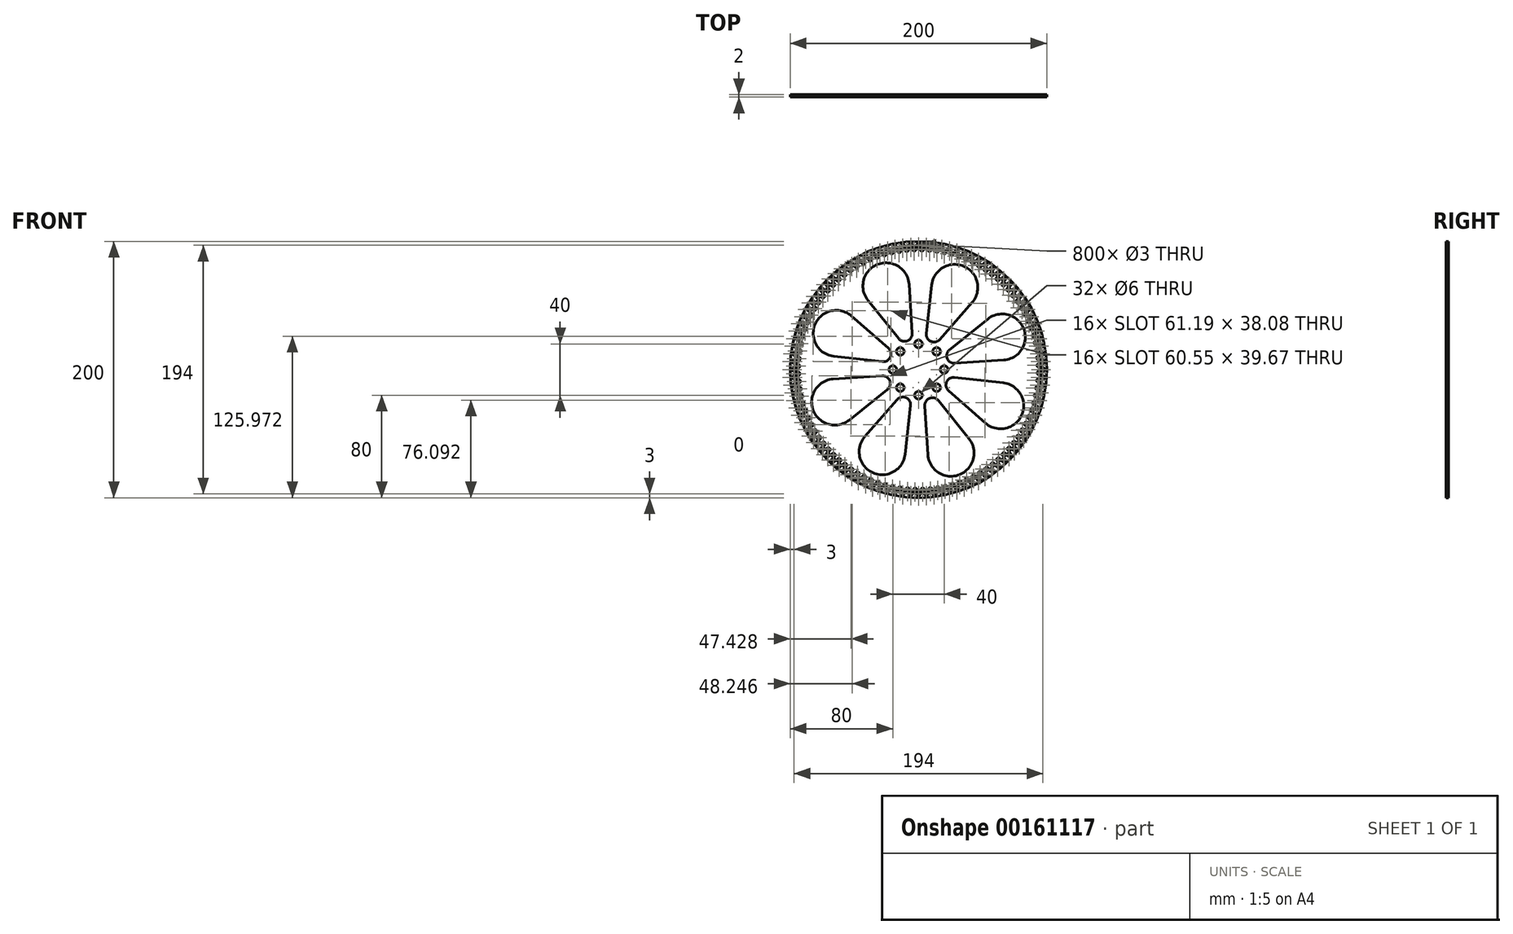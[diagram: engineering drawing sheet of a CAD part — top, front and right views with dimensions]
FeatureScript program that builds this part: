
annotation { "Feature Type Name" : "Feature", "Feature Type Description" : "" }
export const myFeature = defineFeature(function(context is Context, id is Id, definition is map)
    precondition{}
    {
        {
            var Q0;
            Q0=qCreatedBy(makeId("Front.planeOp"),FACE);
            var sketch = newSketch(context, id + "F0", { "sketchPlane" : qUnion([Q0])});
            skCircle(sketch, "E0", {"center": v(0, 0) * mm, "radius": 100 * mm});
            skCircle(sketch, "E1", {"center": v(0, 20) * mm, "radius": 3 * mm});
            skCircle(sketch, "E2.1.0", {"center": v(-14.14, 14.14) * mm, "radius": 3 * mm});
            skCircle(sketch, "E2.2.0", {"center": v(-20, 0) * mm, "radius": 3 * mm});
            skCircle(sketch, "E2.3.0", {"center": v(-14.14, -14.14) * mm, "radius": 3 * mm});
            skCircle(sketch, "E2.4.0", {"center": v(0, -20) * mm, "radius": 3 * mm});
            skCircle(sketch, "E2.5.0", {"center": v(14.14, -14.14) * mm, "radius": 3 * mm});
            skCircle(sketch, "E2.6.0", {"center": v(20, 0) * mm, "radius": 3 * mm});
            skCircle(sketch, "E2.7.0", {"center": v(14.14, 14.14) * mm, "radius": 3 * mm});
            skCircle(sketch, "E3", {"center": v(0, 97) * mm, "radius": 1.5 * mm});
            skCircle(sketch, "E4.1.0", {"center": v(-6.1, 96.8) * mm, "radius": 1.5 * mm});
            skCircle(sketch, "E4.2.0", {"center": v(-12.16, 96.24) * mm, "radius": 1.5 * mm});
            skCircle(sketch, "E4.3.0", {"center": v(-18.18, 95.28) * mm, "radius": 1.5 * mm});
            skCircle(sketch, "E4.4.0", {"center": v(-24.12, 93.95) * mm, "radius": 1.5 * mm});
            skCircle(sketch, "E4.5.0", {"center": v(-29.97, 92.25) * mm, "radius": 1.5 * mm});
            skCircle(sketch, "E4.6.0", {"center": v(-35.7, 90.19) * mm, "radius": 1.5 * mm});
            skCircle(sketch, "E4.7.0", {"center": v(-41.3, 87.77) * mm, "radius": 1.5 * mm});
            skCircle(sketch, "E4.8.0", {"center": v(-46.73, 85) * mm, "radius": 1.5 * mm});
            skCircle(sketch, "E4.9.0", {"center": v(-51.98, 81.9) * mm, "radius": 1.5 * mm});
            skCircle(sketch, "E4.10.0", {"center": v(-57.02, 78.47) * mm, "radius": 1.5 * mm});
            skCircle(sketch, "E4.11.0", {"center": v(-61.83, 74.74) * mm, "radius": 1.5 * mm});
            skCircle(sketch, "E4.12.0", {"center": v(-66.4, 70.7) * mm, "radius": 1.5 * mm});
            skCircle(sketch, "E4.13.0", {"center": v(-70.7, 66.4) * mm, "radius": 1.5 * mm});
            skCircle(sketch, "E4.14.0", {"center": v(-74.74, 61.83) * mm, "radius": 1.5 * mm});
            skCircle(sketch, "E4.15.0", {"center": v(-78.47, 57.02) * mm, "radius": 1.5 * mm});
            skCircle(sketch, "E4.16.0", {"center": v(-81.9, 51.98) * mm, "radius": 1.5 * mm});
            skCircle(sketch, "E4.17.0", {"center": v(-85, 46.73) * mm, "radius": 1.5 * mm});
            skCircle(sketch, "E4.18.0", {"center": v(-87.77, 41.3) * mm, "radius": 1.5 * mm});
            skCircle(sketch, "E4.19.0", {"center": v(-90.19, 35.7) * mm, "radius": 1.5 * mm});
            skCircle(sketch, "E4.20.0", {"center": v(-92.25, 29.97) * mm, "radius": 1.5 * mm});
            skCircle(sketch, "E4.21.0", {"center": v(-93.95, 24.12) * mm, "radius": 1.5 * mm});
            skCircle(sketch, "E4.22.0", {"center": v(-95.28, 18.18) * mm, "radius": 1.5 * mm});
            skCircle(sketch, "E4.23.0", {"center": v(-96.24, 12.16) * mm, "radius": 1.5 * mm});
            skCircle(sketch, "E4.24.0", {"center": v(-96.8, 6.1) * mm, "radius": 1.5 * mm});
            skCircle(sketch, "E4.25.0", {"center": v(-97, 0) * mm, "radius": 1.5 * mm});
            skCircle(sketch, "E4.26.0", {"center": v(-96.8, -6.1) * mm, "radius": 1.5 * mm});
            skCircle(sketch, "E4.27.0", {"center": v(-96.24, -12.16) * mm, "radius": 1.5 * mm});
            skCircle(sketch, "E4.28.0", {"center": v(-95.28, -18.18) * mm, "radius": 1.5 * mm});
            skCircle(sketch, "E4.29.0", {"center": v(-93.95, -24.12) * mm, "radius": 1.5 * mm});
            skCircle(sketch, "E4.30.0", {"center": v(-92.25, -29.97) * mm, "radius": 1.5 * mm});
            skCircle(sketch, "E4.31.0", {"center": v(-90.19, -35.7) * mm, "radius": 1.5 * mm});
            skCircle(sketch, "E4.32.0", {"center": v(-87.77, -41.3) * mm, "radius": 1.5 * mm});
            skCircle(sketch, "E4.33.0", {"center": v(-85, -46.73) * mm, "radius": 1.5 * mm});
            skCircle(sketch, "E4.34.0", {"center": v(-81.9, -51.98) * mm, "radius": 1.5 * mm});
            skCircle(sketch, "E4.35.0", {"center": v(-78.47, -57.02) * mm, "radius": 1.5 * mm});
            skCircle(sketch, "E4.36.0", {"center": v(-74.74, -61.83) * mm, "radius": 1.5 * mm});
            skCircle(sketch, "E4.37.0", {"center": v(-70.7, -66.4) * mm, "radius": 1.5 * mm});
            skCircle(sketch, "E4.38.0", {"center": v(-66.4, -70.7) * mm, "radius": 1.5 * mm});
            skCircle(sketch, "E4.39.0", {"center": v(-61.83, -74.74) * mm, "radius": 1.5 * mm});
            skCircle(sketch, "E4.40.0", {"center": v(-57.02, -78.47) * mm, "radius": 1.5 * mm});
            skCircle(sketch, "E4.41.0", {"center": v(-51.98, -81.9) * mm, "radius": 1.5 * mm});
            skCircle(sketch, "E4.42.0", {"center": v(-46.73, -85) * mm, "radius": 1.5 * mm});
            skCircle(sketch, "E4.43.0", {"center": v(-41.3, -87.77) * mm, "radius": 1.5 * mm});
            skCircle(sketch, "E4.44.0", {"center": v(-35.7, -90.19) * mm, "radius": 1.5 * mm});
            skCircle(sketch, "E4.45.0", {"center": v(-29.97, -92.25) * mm, "radius": 1.5 * mm});
            skCircle(sketch, "E4.46.0", {"center": v(-24.12, -93.95) * mm, "radius": 1.5 * mm});
            skCircle(sketch, "E4.47.0", {"center": v(-18.18, -95.28) * mm, "radius": 1.5 * mm});
            skCircle(sketch, "E4.48.0", {"center": v(-12.16, -96.24) * mm, "radius": 1.5 * mm});
            skCircle(sketch, "E4.49.0", {"center": v(-6.1, -96.8) * mm, "radius": 1.5 * mm});
            skCircle(sketch, "E4.50.0", {"center": v(0, -97) * mm, "radius": 1.5 * mm});
            skCircle(sketch, "E4.51.0", {"center": v(6.1, -96.8) * mm, "radius": 1.5 * mm});
            skCircle(sketch, "E4.52.0", {"center": v(12.16, -96.24) * mm, "radius": 1.5 * mm});
            skCircle(sketch, "E4.53.0", {"center": v(18.18, -95.28) * mm, "radius": 1.5 * mm});
            skCircle(sketch, "E4.54.0", {"center": v(24.12, -93.95) * mm, "radius": 1.5 * mm});
            skCircle(sketch, "E4.55.0", {"center": v(29.97, -92.25) * mm, "radius": 1.5 * mm});
            skCircle(sketch, "E4.56.0", {"center": v(35.7, -90.19) * mm, "radius": 1.5 * mm});
            skCircle(sketch, "E4.57.0", {"center": v(41.3, -87.77) * mm, "radius": 1.5 * mm});
            skCircle(sketch, "E4.58.0", {"center": v(46.73, -85) * mm, "radius": 1.5 * mm});
            skCircle(sketch, "E4.59.0", {"center": v(51.98, -81.9) * mm, "radius": 1.5 * mm});
            skCircle(sketch, "E4.60.0", {"center": v(57.02, -78.47) * mm, "radius": 1.5 * mm});
            skCircle(sketch, "E4.61.0", {"center": v(61.83, -74.74) * mm, "radius": 1.5 * mm});
            skCircle(sketch, "E4.62.0", {"center": v(66.4, -70.7) * mm, "radius": 1.5 * mm});
            skCircle(sketch, "E4.63.0", {"center": v(70.7, -66.4) * mm, "radius": 1.5 * mm});
            skCircle(sketch, "E4.64.0", {"center": v(74.74, -61.83) * mm, "radius": 1.5 * mm});
            skCircle(sketch, "E4.65.0", {"center": v(78.47, -57.02) * mm, "radius": 1.5 * mm});
            skCircle(sketch, "E4.66.0", {"center": v(81.9, -51.98) * mm, "radius": 1.5 * mm});
            skCircle(sketch, "E4.67.0", {"center": v(85, -46.73) * mm, "radius": 1.5 * mm});
            skCircle(sketch, "E4.68.0", {"center": v(87.77, -41.3) * mm, "radius": 1.5 * mm});
            skCircle(sketch, "E4.69.0", {"center": v(90.19, -35.7) * mm, "radius": 1.5 * mm});
            skCircle(sketch, "E4.70.0", {"center": v(92.25, -29.97) * mm, "radius": 1.5 * mm});
            skCircle(sketch, "E4.71.0", {"center": v(93.95, -24.12) * mm, "radius": 1.5 * mm});
            skCircle(sketch, "E4.72.0", {"center": v(95.28, -18.18) * mm, "radius": 1.5 * mm});
            skCircle(sketch, "E4.73.0", {"center": v(96.24, -12.16) * mm, "radius": 1.5 * mm});
            skCircle(sketch, "E4.74.0", {"center": v(96.8, -6.1) * mm, "radius": 1.5 * mm});
            skCircle(sketch, "E4.75.0", {"center": v(97, 0) * mm, "radius": 1.5 * mm});
            skCircle(sketch, "E4.76.0", {"center": v(96.8, 6.1) * mm, "radius": 1.5 * mm});
            skCircle(sketch, "E4.77.0", {"center": v(96.24, 12.16) * mm, "radius": 1.5 * mm});
            skCircle(sketch, "E4.78.0", {"center": v(95.28, 18.18) * mm, "radius": 1.5 * mm});
            skCircle(sketch, "E4.79.0", {"center": v(93.95, 24.12) * mm, "radius": 1.5 * mm});
            skCircle(sketch, "E4.80.0", {"center": v(92.25, 29.97) * mm, "radius": 1.5 * mm});
            skCircle(sketch, "E4.81.0", {"center": v(90.19, 35.7) * mm, "radius": 1.5 * mm});
            skCircle(sketch, "E4.82.0", {"center": v(87.77, 41.3) * mm, "radius": 1.5 * mm});
            skCircle(sketch, "E4.83.0", {"center": v(85, 46.73) * mm, "radius": 1.5 * mm});
            skCircle(sketch, "E4.84.0", {"center": v(81.9, 51.98) * mm, "radius": 1.5 * mm});
            skCircle(sketch, "E4.85.0", {"center": v(78.47, 57.02) * mm, "radius": 1.5 * mm});
            skCircle(sketch, "E4.86.0", {"center": v(74.74, 61.83) * mm, "radius": 1.5 * mm});
            skCircle(sketch, "E4.87.0", {"center": v(70.7, 66.4) * mm, "radius": 1.5 * mm});
            skCircle(sketch, "E4.88.0", {"center": v(66.4, 70.7) * mm, "radius": 1.5 * mm});
            skCircle(sketch, "E4.89.0", {"center": v(61.83, 74.74) * mm, "radius": 1.5 * mm});
            skCircle(sketch, "E4.90.0", {"center": v(57.02, 78.47) * mm, "radius": 1.5 * mm});
            skCircle(sketch, "E4.91.0", {"center": v(51.98, 81.9) * mm, "radius": 1.5 * mm});
            skCircle(sketch, "E4.92.0", {"center": v(46.73, 85) * mm, "radius": 1.5 * mm});
            skCircle(sketch, "E4.93.0", {"center": v(41.3, 87.77) * mm, "radius": 1.5 * mm});
            skCircle(sketch, "E4.94.0", {"center": v(35.7, 90.19) * mm, "radius": 1.5 * mm});
            skCircle(sketch, "E4.95.0", {"center": v(29.97, 92.25) * mm, "radius": 1.5 * mm});
            skCircle(sketch, "E4.96.0", {"center": v(24.12, 93.95) * mm, "radius": 1.5 * mm});
            skCircle(sketch, "E4.97.0", {"center": v(18.18, 95.28) * mm, "radius": 1.5 * mm});
            skCircle(sketch, "E4.98.0", {"center": v(12.16, 96.24) * mm, "radius": 1.5 * mm});
            skCircle(sketch, "E4.99.0", {"center": v(6.1, 96.8) * mm, "radius": 1.5 * mm});
            skCircle(sketch, "E5", {"center": v(2.62, 93.96) * mm, "radius": 1.5 * mm});
            skLineSegment(sketch, "E6", {"start": v(0, 97) * mm, "end": v(0, 0) * mm, "construction": true});
            skLineSegment(sketch, "E7", {"start": v(2.62, 93.96) * mm, "end": v(0, 0) * mm, "construction": true});
            skCircle(sketch, "E8.1.0", {"center": v(-3.28, 93.94) * mm, "radius": 1.5 * mm});
            skCircle(sketch, "E8.2.0", {"center": v(-9.17, 93.55) * mm, "radius": 1.5 * mm});
            skCircle(sketch, "E9.1.3.0", {"center": v(-15.03, 92.8) * mm, "radius": 1.5 * mm});
            skCircle(sketch, "E9.1.4.0", {"center": v(-20.83, 91.66) * mm, "radius": 1.5 * mm});
            skCircle(sketch, "E9.1.5.0", {"center": v(-26.54, 90.18) * mm, "radius": 1.5 * mm});
            skCircle(sketch, "E9.1.6.0", {"center": v(-32.15, 88.33) * mm, "radius": 1.5 * mm});
            skCircle(sketch, "E9.1.7.0", {"center": v(-37.63, 86.14) * mm, "radius": 1.5 * mm});
            skCircle(sketch, "E9.1.8.0", {"center": v(-42.97, 83.6) * mm, "radius": 1.5 * mm});
            skCircle(sketch, "E9.1.9.0", {"center": v(-48.13, 80.74) * mm, "radius": 1.5 * mm});
            skCircle(sketch, "E9.1.10.0", {"center": v(-53.1, 77.56) * mm, "radius": 1.5 * mm});
            skCircle(sketch, "E9.1.11.0", {"center": v(-57.87, 74.07) * mm, "radius": 1.5 * mm});
            skCircle(sketch, "E9.1.12.0", {"center": v(-62.4, 70.3) * mm, "radius": 1.5 * mm});
            skCircle(sketch, "E9.1.13.0", {"center": v(-66.7, 66.24) * mm, "radius": 1.5 * mm});
            skCircle(sketch, "E9.1.14.0", {"center": v(-70.73, 61.92) * mm, "radius": 1.5 * mm});
            skCircle(sketch, "E9.1.15.0", {"center": v(-74.48, 57.35) * mm, "radius": 1.5 * mm});
            skCircle(sketch, "E9.1.16.0", {"center": v(-77.93, 52.56) * mm, "radius": 1.5 * mm});
            skCircle(sketch, "E9.1.17.0", {"center": v(-81.08, 47.57) * mm, "radius": 1.5 * mm});
            skCircle(sketch, "E9.1.18.0", {"center": v(-83.9, 42.38) * mm, "radius": 1.5 * mm});
            skCircle(sketch, "E9.1.19.0", {"center": v(-86.4, 37.03) * mm, "radius": 1.5 * mm});
            skCircle(sketch, "E9.1.20.0", {"center": v(-88.55, 31.53) * mm, "radius": 1.5 * mm});
            skCircle(sketch, "E9.1.21.0", {"center": v(-90.36, 25.9) * mm, "radius": 1.5 * mm});
            skCircle(sketch, "E9.1.22.0", {"center": v(-91.8, 20.19) * mm, "radius": 1.5 * mm});
            skCircle(sketch, "E9.1.23.0", {"center": v(-92.9, 14.38) * mm, "radius": 1.5 * mm});
            skCircle(sketch, "E9.1.24.0", {"center": v(-93.61, 8.52) * mm, "radius": 1.5 * mm});
            skCircle(sketch, "E9.1.25.0", {"center": v(-93.96, 2.62) * mm, "radius": 1.5 * mm});
            skCircle(sketch, "E9.1.26.0", {"center": v(-93.94, -3.28) * mm, "radius": 1.5 * mm});
            skCircle(sketch, "E9.1.27.0", {"center": v(-93.55, -9.17) * mm, "radius": 1.5 * mm});
            skCircle(sketch, "E9.1.28.0", {"center": v(-92.8, -15.03) * mm, "radius": 1.5 * mm});
            skCircle(sketch, "E9.1.29.0", {"center": v(-91.66, -20.83) * mm, "radius": 1.5 * mm});
            skCircle(sketch, "E9.1.30.0", {"center": v(-90.18, -26.54) * mm, "radius": 1.5 * mm});
            skCircle(sketch, "E9.1.31.0", {"center": v(-88.33, -32.15) * mm, "radius": 1.5 * mm});
            skCircle(sketch, "E9.1.32.0", {"center": v(-86.14, -37.63) * mm, "radius": 1.5 * mm});
            skCircle(sketch, "E9.1.33.0", {"center": v(-83.6, -42.97) * mm, "radius": 1.5 * mm});
            skCircle(sketch, "E9.1.34.0", {"center": v(-80.74, -48.13) * mm, "radius": 1.5 * mm});
            skCircle(sketch, "E9.1.35.0", {"center": v(-77.56, -53.1) * mm, "radius": 1.5 * mm});
            skCircle(sketch, "E9.1.36.0", {"center": v(-74.07, -57.87) * mm, "radius": 1.5 * mm});
            skCircle(sketch, "E9.1.37.0", {"center": v(-70.3, -62.4) * mm, "radius": 1.5 * mm});
            skCircle(sketch, "E9.1.38.0", {"center": v(-66.24, -66.7) * mm, "radius": 1.5 * mm});
            skCircle(sketch, "E9.1.39.0", {"center": v(-61.92, -70.73) * mm, "radius": 1.5 * mm});
            skCircle(sketch, "E9.1.40.0", {"center": v(-57.35, -74.48) * mm, "radius": 1.5 * mm});
            skCircle(sketch, "E9.1.41.0", {"center": v(-52.56, -77.93) * mm, "radius": 1.5 * mm});
            skCircle(sketch, "E9.1.42.0", {"center": v(-47.57, -81.08) * mm, "radius": 1.5 * mm});
            skCircle(sketch, "E9.1.43.0", {"center": v(-42.38, -83.9) * mm, "radius": 1.5 * mm});
            skCircle(sketch, "E9.1.44.0", {"center": v(-37.03, -86.4) * mm, "radius": 1.5 * mm});
            skCircle(sketch, "E9.1.45.0", {"center": v(-31.53, -88.55) * mm, "radius": 1.5 * mm});
            skCircle(sketch, "E9.1.46.0", {"center": v(-25.9, -90.36) * mm, "radius": 1.5 * mm});
            skCircle(sketch, "E9.1.47.0", {"center": v(-20.19, -91.8) * mm, "radius": 1.5 * mm});
            skCircle(sketch, "E9.1.48.0", {"center": v(-14.38, -92.9) * mm, "radius": 1.5 * mm});
            skCircle(sketch, "E9.1.49.0", {"center": v(-8.52, -93.61) * mm, "radius": 1.5 * mm});
            skCircle(sketch, "E9.1.50.0", {"center": v(-2.62, -93.96) * mm, "radius": 1.5 * mm});
            skCircle(sketch, "E9.1.51.0", {"center": v(3.28, -93.94) * mm, "radius": 1.5 * mm});
            skCircle(sketch, "E9.1.52.0", {"center": v(9.17, -93.55) * mm, "radius": 1.5 * mm});
            skCircle(sketch, "E9.1.53.0", {"center": v(15.03, -92.8) * mm, "radius": 1.5 * mm});
            skCircle(sketch, "E9.1.54.0", {"center": v(20.83, -91.66) * mm, "radius": 1.5 * mm});
            skCircle(sketch, "E9.1.55.0", {"center": v(26.54, -90.18) * mm, "radius": 1.5 * mm});
            skCircle(sketch, "E9.1.56.0", {"center": v(32.15, -88.33) * mm, "radius": 1.5 * mm});
            skCircle(sketch, "E9.1.57.0", {"center": v(37.63, -86.14) * mm, "radius": 1.5 * mm});
            skCircle(sketch, "E9.1.58.0", {"center": v(42.97, -83.6) * mm, "radius": 1.5 * mm});
            skCircle(sketch, "E9.1.59.0", {"center": v(48.13, -80.74) * mm, "radius": 1.5 * mm});
            skCircle(sketch, "E9.1.60.0", {"center": v(53.1, -77.56) * mm, "radius": 1.5 * mm});
            skCircle(sketch, "E9.1.61.0", {"center": v(57.87, -74.07) * mm, "radius": 1.5 * mm});
            skCircle(sketch, "E9.1.62.0", {"center": v(62.4, -70.3) * mm, "radius": 1.5 * mm});
            skCircle(sketch, "E9.1.63.0", {"center": v(66.7, -66.24) * mm, "radius": 1.5 * mm});
            skCircle(sketch, "E9.1.64.0", {"center": v(70.73, -61.92) * mm, "radius": 1.5 * mm});
            skCircle(sketch, "E9.1.65.0", {"center": v(74.48, -57.35) * mm, "radius": 1.5 * mm});
            skCircle(sketch, "E9.1.66.0", {"center": v(77.93, -52.56) * mm, "radius": 1.5 * mm});
            skCircle(sketch, "E9.1.67.0", {"center": v(81.08, -47.57) * mm, "radius": 1.5 * mm});
            skCircle(sketch, "E9.1.68.0", {"center": v(83.9, -42.38) * mm, "radius": 1.5 * mm});
            skCircle(sketch, "E9.1.69.0", {"center": v(86.4, -37.03) * mm, "radius": 1.5 * mm});
            skCircle(sketch, "E9.1.70.0", {"center": v(88.55, -31.53) * mm, "radius": 1.5 * mm});
            skCircle(sketch, "E9.1.71.0", {"center": v(90.36, -25.9) * mm, "radius": 1.5 * mm});
            skCircle(sketch, "E9.1.72.0", {"center": v(91.8, -20.19) * mm, "radius": 1.5 * mm});
            skCircle(sketch, "E9.1.73.0", {"center": v(92.9, -14.38) * mm, "radius": 1.5 * mm});
            skCircle(sketch, "E9.1.74.0", {"center": v(93.61, -8.52) * mm, "radius": 1.5 * mm});
            skCircle(sketch, "E9.1.75.0", {"center": v(93.96, -2.62) * mm, "radius": 1.5 * mm});
            skCircle(sketch, "E9.1.76.0", {"center": v(93.94, 3.28) * mm, "radius": 1.5 * mm});
            skCircle(sketch, "E9.1.77.0", {"center": v(93.55, 9.17) * mm, "radius": 1.5 * mm});
            skCircle(sketch, "E9.1.78.0", {"center": v(92.8, 15.03) * mm, "radius": 1.5 * mm});
            skCircle(sketch, "E9.1.79.0", {"center": v(91.66, 20.83) * mm, "radius": 1.5 * mm});
            skCircle(sketch, "E9.1.80.0", {"center": v(90.18, 26.54) * mm, "radius": 1.5 * mm});
            skCircle(sketch, "E9.1.81.0", {"center": v(88.33, 32.15) * mm, "radius": 1.5 * mm});
            skCircle(sketch, "E9.1.82.0", {"center": v(86.14, 37.63) * mm, "radius": 1.5 * mm});
            skCircle(sketch, "E9.1.83.0", {"center": v(83.6, 42.97) * mm, "radius": 1.5 * mm});
            skCircle(sketch, "E9.1.84.0", {"center": v(80.74, 48.13) * mm, "radius": 1.5 * mm});
            skCircle(sketch, "E9.1.85.0", {"center": v(77.56, 53.1) * mm, "radius": 1.5 * mm});
            skCircle(sketch, "E9.1.86.0", {"center": v(74.07, 57.87) * mm, "radius": 1.5 * mm});
            skCircle(sketch, "E9.1.87.0", {"center": v(70.3, 62.4) * mm, "radius": 1.5 * mm});
            skCircle(sketch, "E9.1.88.0", {"center": v(66.24, 66.7) * mm, "radius": 1.5 * mm});
            skCircle(sketch, "E9.1.89.0", {"center": v(61.92, 70.73) * mm, "radius": 1.5 * mm});
            skCircle(sketch, "E9.1.90.0", {"center": v(57.35, 74.48) * mm, "radius": 1.5 * mm});
            skCircle(sketch, "E9.1.91.0", {"center": v(52.56, 77.93) * mm, "radius": 1.5 * mm});
            skCircle(sketch, "E9.1.92.0", {"center": v(47.57, 81.08) * mm, "radius": 1.5 * mm});
            skCircle(sketch, "E9.1.93.0", {"center": v(42.38, 83.9) * mm, "radius": 1.5 * mm});
            skCircle(sketch, "E9.1.94.0", {"center": v(37.03, 86.4) * mm, "radius": 1.5 * mm});
            skCircle(sketch, "E9.1.95.0", {"center": v(31.53, 88.55) * mm, "radius": 1.5 * mm});
            skCircle(sketch, "E9.1.96.0", {"center": v(25.9, 90.36) * mm, "radius": 1.5 * mm});
            skCircle(sketch, "E9.1.97.0", {"center": v(20.19, 91.8) * mm, "radius": 1.5 * mm});
            skCircle(sketch, "E9.1.98.0", {"center": v(14.38, 92.9) * mm, "radius": 1.5 * mm});
            skCircle(sketch, "E9.1.99.0", {"center": v(8.52, 93.61) * mm, "radius": 1.5 * mm});
            skArc(sketch, "E10", {"start": v(-28.11, 6.14) * mm, "mid": v(-21.96, 9.68) * mm, "end": v(-23.5, 16.61) * mm});
            skArc(sketch, "E11", {"start": v(-52.19, 41.77) * mm, "mid": v(-80.52, 35.5) * mm, "end": v(-66.04, 10.34) * mm});
            skLineSegment(sketch, "E12", {"start": v(-28.11, 6.14) * mm, "end": v(-66.04, 10.34) * mm});
            skLineSegment(sketch, "E13", {"start": v(-23.5, 16.61) * mm, "end": v(-52.19, 41.77) * mm});
            skLineSegment(sketch, "E14", {"start": v(0, 0) * mm, "end": v(-91.5, 40.33) * mm, "construction": true});
            skLineSegment(sketch, "E15.1.0", {"start": v(-24.22, -15.54) * mm, "end": v(-54, -39.38) * mm});
            skArc(sketch, "E15.1.1", {"start": v(-66.44, -7.37) * mm, "mid": v(-82.04, -31.84) * mm, "end": v(-54, -39.38) * mm});
            skLineSegment(sketch, "E15.1.2", {"start": v(-28.36, -4.87) * mm, "end": v(-66.44, -7.37) * mm});
            skArc(sketch, "E15.1.3", {"start": v(-24.22, -15.54) * mm, "mid": v(-22.37, -8.68) * mm, "end": v(-28.36, -4.87) * mm});
            skLineSegment(sketch, "E15.2.0", {"start": v(-6.14, -28.11) * mm, "end": v(-10.34, -66.04) * mm});
            skArc(sketch, "E15.2.1", {"start": v(-41.77, -52.19) * mm, "mid": v(-35.5, -80.52) * mm, "end": v(-10.34, -66.04) * mm});
            skLineSegment(sketch, "E15.2.2", {"start": v(-16.61, -23.5) * mm, "end": v(-41.77, -52.19) * mm});
            skArc(sketch, "E15.2.3", {"start": v(-6.14, -28.11) * mm, "mid": v(-9.68, -21.96) * mm, "end": v(-16.61, -23.5) * mm});
            skLineSegment(sketch, "E15.3.0", {"start": v(15.54, -24.22) * mm, "end": v(39.38, -54) * mm});
            skArc(sketch, "E15.3.1", {"start": v(7.37, -66.44) * mm, "mid": v(31.84, -82.04) * mm, "end": v(39.38, -54) * mm});
            skLineSegment(sketch, "E15.3.2", {"start": v(4.87, -28.36) * mm, "end": v(7.37, -66.44) * mm});
            skArc(sketch, "E15.3.3", {"start": v(15.54, -24.22) * mm, "mid": v(8.68, -22.37) * mm, "end": v(4.87, -28.36) * mm});
            skLineSegment(sketch, "E15.4.0", {"start": v(28.11, -6.14) * mm, "end": v(66.04, -10.34) * mm});
            skArc(sketch, "E15.4.1", {"start": v(52.19, -41.77) * mm, "mid": v(80.52, -35.5) * mm, "end": v(66.04, -10.34) * mm});
            skLineSegment(sketch, "E15.4.2", {"start": v(23.5, -16.61) * mm, "end": v(52.19, -41.77) * mm});
            skArc(sketch, "E15.4.3", {"start": v(28.11, -6.14) * mm, "mid": v(21.96, -9.68) * mm, "end": v(23.5, -16.61) * mm});
            skLineSegment(sketch, "E15.5.0", {"start": v(24.22, 15.54) * mm, "end": v(54, 39.38) * mm});
            skArc(sketch, "E15.5.1", {"start": v(66.44, 7.37) * mm, "mid": v(82.04, 31.84) * mm, "end": v(54, 39.38) * mm});
            skLineSegment(sketch, "E15.5.2", {"start": v(28.36, 4.87) * mm, "end": v(66.44, 7.37) * mm});
            skArc(sketch, "E15.5.3", {"start": v(24.22, 15.54) * mm, "mid": v(22.37, 8.68) * mm, "end": v(28.36, 4.87) * mm});
            skLineSegment(sketch, "E15.6.0", {"start": v(6.14, 28.11) * mm, "end": v(10.34, 66.04) * mm});
            skArc(sketch, "E15.6.1", {"start": v(41.77, 52.19) * mm, "mid": v(35.5, 80.52) * mm, "end": v(10.34, 66.04) * mm});
            skLineSegment(sketch, "E15.6.2", {"start": v(16.61, 23.5) * mm, "end": v(41.77, 52.19) * mm});
            skArc(sketch, "E15.6.3", {"start": v(6.14, 28.11) * mm, "mid": v(9.68, 21.96) * mm, "end": v(16.61, 23.5) * mm});
            skLineSegment(sketch, "E15.7.0", {"start": v(-15.54, 24.22) * mm, "end": v(-39.38, 54) * mm});
            skArc(sketch, "E15.7.1", {"start": v(-7.37, 66.44) * mm, "mid": v(-31.84, 82.04) * mm, "end": v(-39.38, 54) * mm});
            skLineSegment(sketch, "E15.7.2", {"start": v(-4.87, 28.36) * mm, "end": v(-7.37, 66.44) * mm});
            skArc(sketch, "E15.7.3", {"start": v(-15.54, 24.22) * mm, "mid": v(-8.68, 22.37) * mm, "end": v(-4.87, 28.36) * mm});
            skSolve(sketch);
        }
        {
            var Q0;
            Q0 = qSketchRegion(id + "F0", true);
            extrude(context, id + "F1", {"entities" : qUnion([Q0]), "depth" : 2 * mm});
        }
    });
